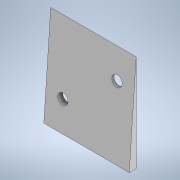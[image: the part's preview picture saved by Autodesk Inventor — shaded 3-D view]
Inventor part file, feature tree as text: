
AUTODESK INVENTOR PART (.ipt)
format: ipt  version: 2021 (Build 250183000, 183)  size: 102,400 bytes
history: native  units: mm
features: sketch x2, extrude x1, hole x1, projected_geometry x1
ambient origin geometry x8: Origin, YZ Plane, XZ Plane, XY Plane, X Axis, Y Axis, Z Axis, Center Point
bodies: Solid1 (feature_tree)
feature tree (5):
  extrude  "Extrusion1"  Depth=85.0mm
  hole  "Hole1"  [1 undecoded]
  sketch  "Sketch1"  dims[d0=0.71384mm d1=85.0mm]
  sketch  "Sketch2"  dims[d2=75.0mm d3=0.0mm d4=25.0mm d5=15.0mm d6=15.0mm d7=25.0mm d8=9.0mm d9=6.0mm d10=15.0mm d11=9.0mm d12=90.0deg d13=10.0mm d14=20.594885mm]
  projected_geometry  "Projected Loop1"
note: 1 required parameter value undecoded (feature->parameter linkage not recoverable at this tier; creation-order binding heuristic only, values carry confidence <= 0.55)
